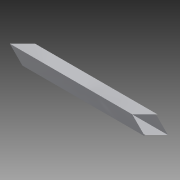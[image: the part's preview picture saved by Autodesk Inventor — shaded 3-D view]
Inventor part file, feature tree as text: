
AUTODESK INVENTOR PART (.ipt)
format: ipt  version: 2014 (Build 180170000, 170)  size: 90,624 bytes
history: native  units: in
note: dims shown in document units (in); Inventor stores cm internally (conversion verified against a paired STEP export)
features: extrude x1, sketch x1
ambient origin geometry x8: Origin, YZ Plane, XZ Plane, XY Plane, X Axis, Y Axis, Z Axis, Center Point
bodies: Solid1 (feature_tree)
feature tree (2):
  extrude  "Extrusion1"  Depth=1.0in
  sketch  "Sketch1"  dims[d0=1.0in d1=1.0in d2=0.0625in d3=12.0in d4=0.0in]
